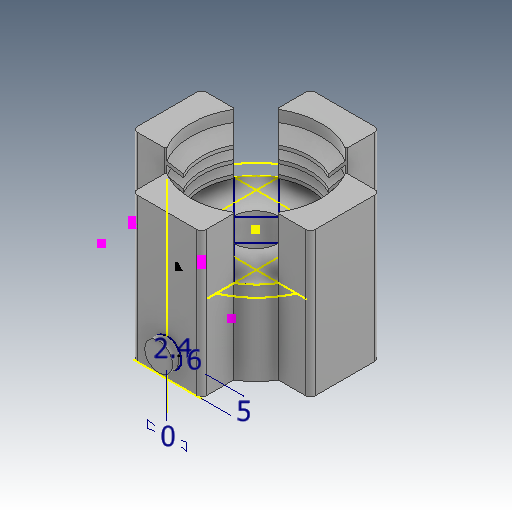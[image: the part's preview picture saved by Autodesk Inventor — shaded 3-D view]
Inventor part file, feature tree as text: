
AUTODESK INVENTOR PART (.ipt)
format: ipt  version: 2021.3 (Build 253353000, 353)  size: 376,320 bytes
history: native  units: mm
features: extrude x10, sketch x5, revolve x1, mirror x1, hole x1, fillet x1
ambient origin geometry x8: Origin, YZ Plane, XZ Plane, XY Plane, X Axis, Y Axis, Z Axis, Center Point
bodies: Solid1 (feature_tree)
feature tree (19):
  revolve  "Revolution1"  [1 undecoded]
  sketch  "Sketch3"  dims[d4=0.0mm d5=17.78mm]
  extrude  "Extrusion1"  Depth=17.78mm
  extrude  "Extrusion2"  Depth=15.875mm
  extrude  "Extrusion4"  Depth=5.175mm
  extrude  "Extrusion9"  TaperAngle=45.0deg  [1 undecoded]
  sketch  "Sketch5"  dims[d6=0.0mm d7=15.875mm]
  extrude  "Extrusion6"  Depth=2.0mm
  extrude  "Extrusion8"  Depth=0.75mm
  mirror  "Mirror1"
  hole  "Hole1"  [1 undecoded]
  extrude  "Extrusion10"  Depth=0.75mm
  extrude  "Extrusion11"  Depth=2.0mm
  fillet  "Fillet1"  Radius=0.75mm
  sketch  "Sketch8"  dims[d10=2.0mm d11=45.0deg d12=2.0mm d13=0.75mm d14=45.0deg d15=0.75mm d21=2.0mm d23=0.75mm d24=90.0deg d25=3.0mm d26=0.0mm d27=7.45mm d28=0.0mm d29=0.0mm d32=10.0mm d33=0.0mm d38=1.8mm d39=0.0mm d42=0.5mm d43=0.0mm d44=3.0mm d45=15.2mm d46=0.0mm d50=5.3mm d51=6.0mm d52=10.0mm d53=12.0mm d54=90.0deg d55=8.0mm d56=20.594885mm d60=6.0mm d61=0.0mm d63=5.0mm d64=2.4mm d65=7.45mm d66=0.0mm d67=3.0mm d68=15.875mm d69=0.0mm d70=10.0mm d71=0.0mm d72=1.0mm d73=28.73603mm d74=0.0mm d75=0.0mm d76=10.0mm d77=0.0mm]
  extrude  "Extrusion12"  TaperAngle=90.0deg  [1 undecoded]
  extrude  "Extrusion13"  Depth=3.0mm TaperAngle=0.0deg
  sketch  "Sketch2"  dims[d2=11.557mm d3=13.97mm]
  sketch  "Sketch7"  dims[d8=3.81mm d9=5.175mm]
note: 4 required parameter values undecoded (feature->parameter linkage not recoverable at this tier; creation-order binding heuristic only, values carry confidence <= 0.55)